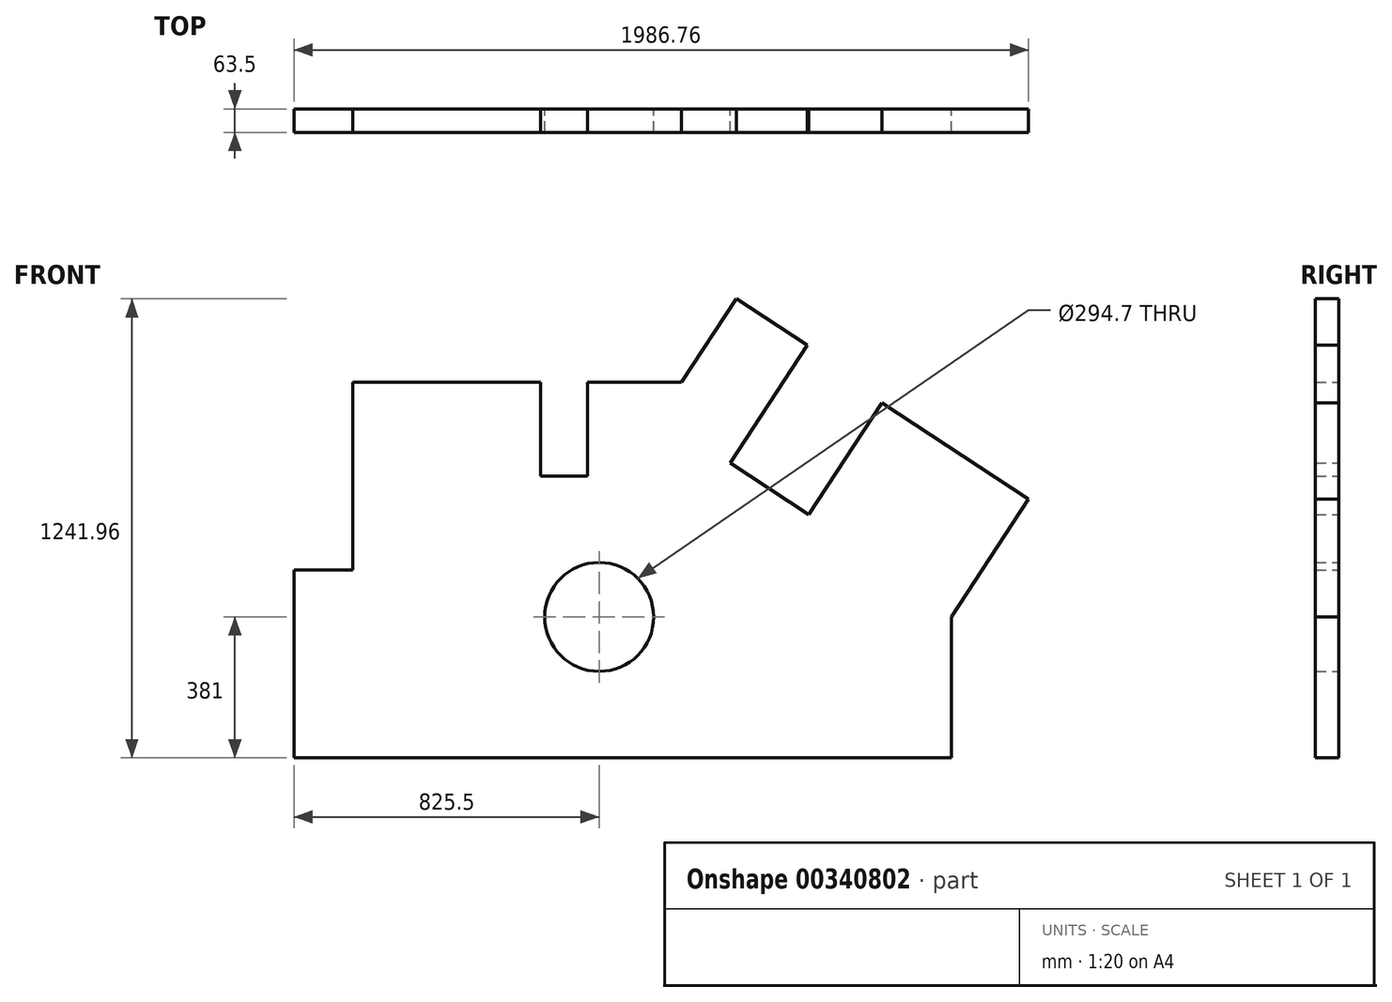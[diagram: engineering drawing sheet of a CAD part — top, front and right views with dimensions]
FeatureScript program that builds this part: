
annotation { "Feature Type Name" : "Feature", "Feature Type Description" : "" }
export const myFeature = defineFeature(function(context is Context, id is Id, definition is map)
    precondition{}
    {
        {
            var Q0;
            Q0=qCreatedBy(makeId("Front.planeOp"),FACE);
            var sketch = newSketch(context, id + "F0", { "sketchPlane" : qUnion([Q0])});
            skLineSegment(sketch, "E0", {"start": v(-60.92, 635) * mm, "end": v(447.08, 635) * mm});
            skLineSegment(sketch, "E1", {"start": v(447.08, 635) * mm, "end": v(447.08, 381) * mm});
            skLineSegment(sketch, "E2", {"start": v(447.08, 381) * mm, "end": v(574.08, 381) * mm});
            skLineSegment(sketch, "E3", {"start": v(574.08, 381) * mm, "end": v(574.08, 635) * mm});
            skLineSegment(sketch, "E4", {"start": v(574.08, 635) * mm, "end": v(828.08, 635) * mm});
            skLineSegment(sketch, "E5", {"start": v(828.08, 635) * mm, "end": v(976.09, 860.96) * mm});
            skLineSegment(sketch, "E6", {"start": v(976.09, 860.96) * mm, "end": v(1168.34, 735.04) * mm});
            skLineSegment(sketch, "E7", {"start": v(1168.34, 735.04) * mm, "end": v(959.58, 416.32) * mm});
            skLineSegment(sketch, "E8", {"start": v(959.58, 416.32) * mm, "end": v(1172.05, 277.15) * mm});
            skLineSegment(sketch, "E9", {"start": v(-60.92, 635) * mm, "end": v(-60.92, 127) * mm});
            skLineSegment(sketch, "E10", {"start": v(-60.92, 127) * mm, "end": v(-220.13, 127) * mm});
            skLineSegment(sketch, "E11", {"start": v(-220.13, 127) * mm, "end": v(-220.13, -381) * mm});
            skLineSegment(sketch, "E12", {"start": v(-220.13, -381) * mm, "end": v(1557.87, -381) * mm});
            skLineSegment(sketch, "E13", {"start": v(1172.05, 277.15) * mm, "end": v(1369.61, 578.76) * mm});
            skLineSegment(sketch, "E14", {"start": v(1369.61, 578.76) * mm, "end": v(1766.63, 318.72) * mm});
            skLineSegment(sketch, "E15", {"start": v(1766.63, 318.72) * mm, "end": v(1557.87, 0) * mm});
            skLineSegment(sketch, "E16", {"start": v(1557.87, 0) * mm, "end": v(1557.87, -381) * mm});
            skCircle(sketch, "E17", {"center": v(605.37, 0) * mm, "radius": 147.35 * mm});
            skSolve(sketch);
        }
        {
            var Q0;
            Q0=makeQuery(id+"F0.imprint","IMPRINT",FACE,{"disambiguationData":[TD([[makeQuery(id+"F0.imprint","IMPRINT",EDGE,{"derivedFrom":sQuery(id+"F0.wireOp",EDGE,"E0")}),-1.0]])]});
            extrude(context, id + "F1", {"entities" : qUnion([Q0]), "depth" : 63.5 * mm});
        }
    });
